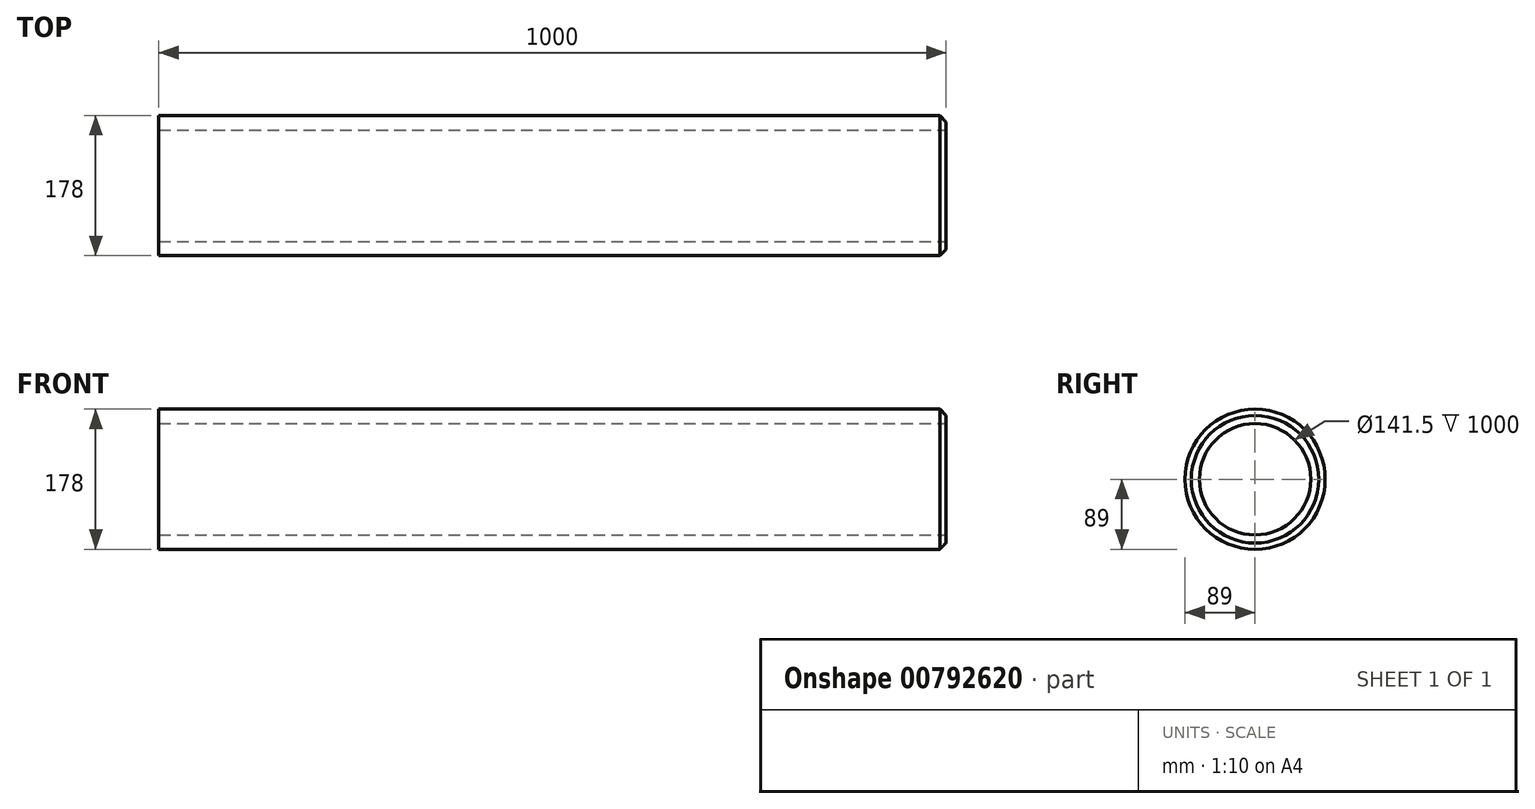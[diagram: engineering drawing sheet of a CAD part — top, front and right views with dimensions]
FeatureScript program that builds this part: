
annotation { "Feature Type Name" : "Feature", "Feature Type Description" : "" }
export const myFeature = defineFeature(function(context is Context, id is Id, definition is map)
    precondition{}
    {
        {
            var Q0;
            Q0=qCreatedBy(makeId("Right.planeOp"),FACE);
            var sketch = newSketch(context, id + "F0", { "sketchPlane" : qUnion([Q0])});
            skCircle(sketch, "E0", {"center": v(0, 0) * mm, "radius": 89 * mm});
            skCircle(sketch, "E1", {"center": v(0, 0) * mm, "radius": 70.75 * mm});
            skSolve(sketch);
        }
        {
            var Q0;
            Q0=makeQuery(id+"F0.imprint","IMPRINT",FACE,{"disambiguationData":[TD([[makeQuery(id+"F0.imprint","IMPRINT",EDGE,{"derivedFrom":sQuery(id+"F0.wireOp",EDGE,"E0")}),1.0]])]});
            extrude(context, id + "F1", {"entities" : qUnion([Q0]), "oppositeDirection" : true, "depth" : 1000 * mm, "offsetDistance" : 25 * mm});
        }
        {
            var Q0;
            Q0=makeQuery(id+"F1.opExtrude","CAP_EDGE",EDGE,{"disambiguationData":[OSD([sQuery(id+"F0.wireOp",EDGE,"E0")])],"isStart":true});
            chamfer(context, id + "F2", {"entities" : qUnion([Q0]), "width" : 8 * mm, "tangentPropagation" : true});
        }
    });
